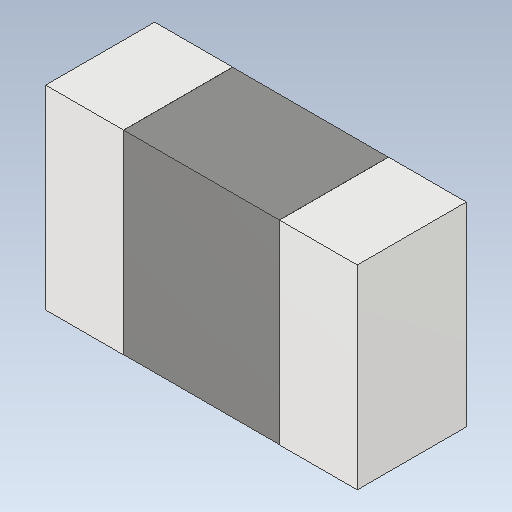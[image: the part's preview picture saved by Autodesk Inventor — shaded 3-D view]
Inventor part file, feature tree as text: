
AUTODESK INVENTOR PART (.ipt)
format: ipt  version: 2020 (Build 240168000, 168)  size: 92,672 bytes
history: imported  units: in
note: dims shown in document units (in); Inventor stores cm internally (conversion verified against a paired STEP export)
features: imported_body x1
ambient origin geometry x8: Origin, YZ Plane, XZ Plane, XY Plane, X Axis, Y Axis, Z Axis, Center Point
bodies: Solid1 (imported_parasolid), Body2 (imported_parasolid)
feature tree (1):
  imported_body  NMx_Import_Brep_tag  [imported B-rep: ~14 faces, bbox_mm=[2.0, 1.25, 0.7]]
